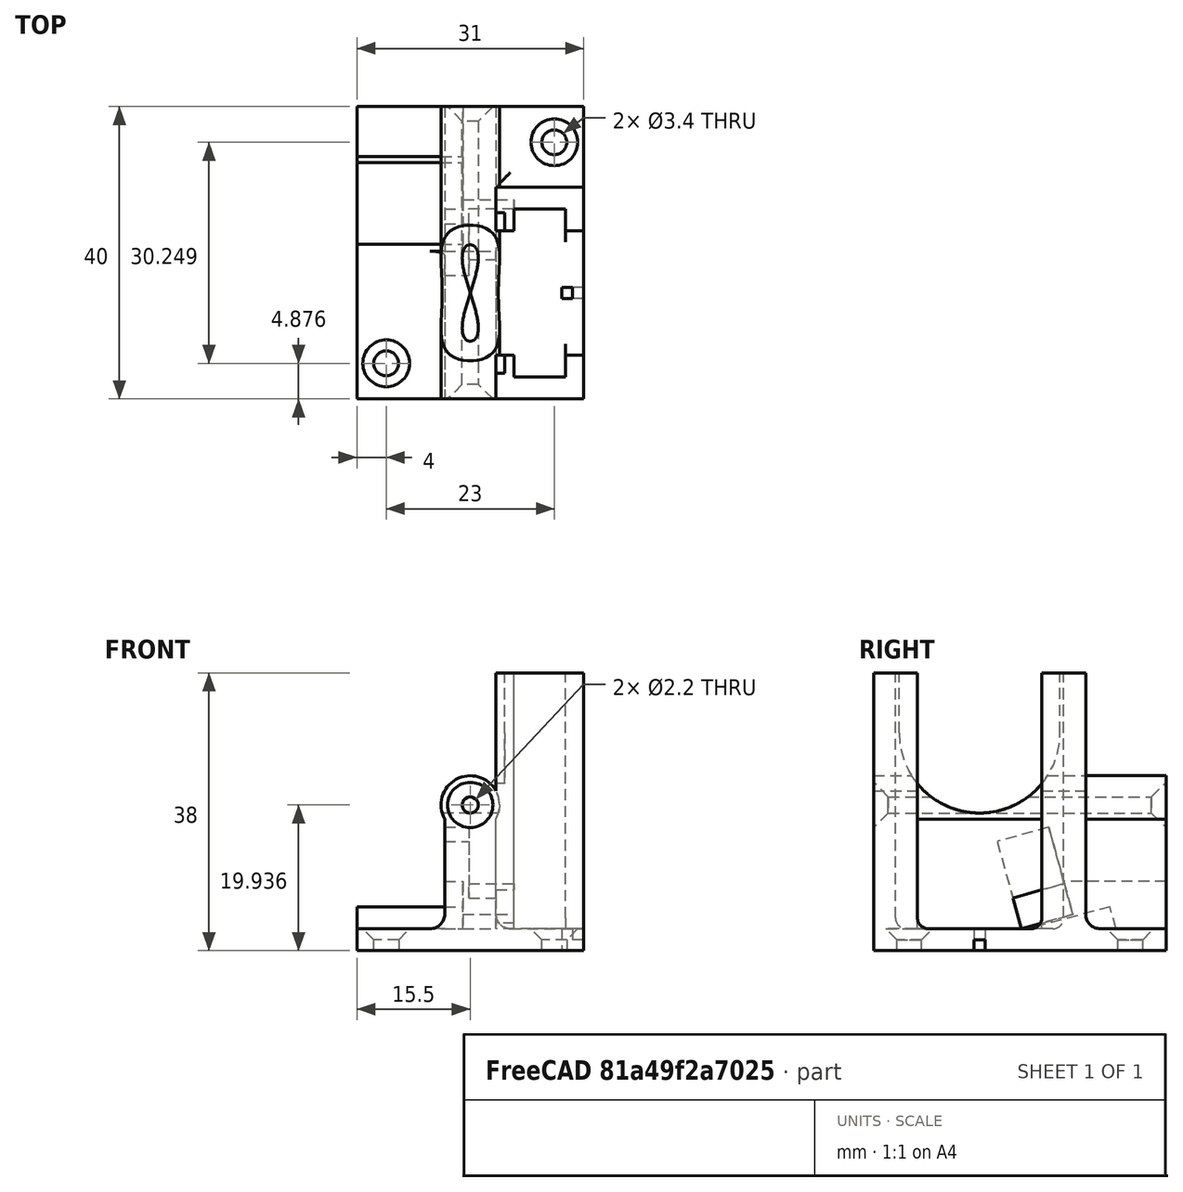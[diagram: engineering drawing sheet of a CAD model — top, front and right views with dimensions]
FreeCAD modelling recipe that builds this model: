
FCSTD DOCUMENT  (FreeCAD 0.20RUnknown)
Label: MainBody
License: All rights reserved
LicenseURL: http://en.wikipedia.org/wiki/All_rights_reserved
objects: Sketcher::SketchObject×10, PartDesign::Pocket×7, PartDesign::Pad×3, PartDesign::Fillet×2, PartDesign::Chamfer×2, Mesh::Feature×1, App::Part×1, PartDesign::Body×1
note: 39 computed .brp shape members not serialized (recipe doc carries the construction recipe); baked Part::Feature solids carry a one-line shape summary decoded from their .brp
EXTERNAL_REF file=SharedParameters.FCStd obj=Spreadsheet

FEATURE [Sketcher::SketchObject] Sketch  label="MainBodySketch"
  FullyConstrained = true
  MapMode = 5
  Placement = pos=(0,0,0) rot=(1,0,0;1.5708rad)
  Support = -> [XZ_Plane]
  expr: Constraints[19] = <<SharedParameters>>#<<Parameters>>.WallThinkness
  expr: Constraints[20] = <<SharedParameters>>#<<Parameters>>.FilamentWheel_BaseWidth
  sketch-geometry (9):
    g0: LineSegment StartX=-15.5 StartY=0 StartZ=0 EndX=-15.5 EndY=3 EndZ=0
    g1: LineSegment StartX=-15.5 StartY=3 StartZ=0 EndX=-3.5 EndY=3 EndZ=0
    g2: LineSegment StartX=-3.5 StartY=3 StartZ=0 EndX=-3.5 EndY=18 EndZ=0
    g3: LineSegment StartX=-15.5 StartY=0 StartZ=0 EndX=15.5 EndY=0 EndZ=0
    g4: LineSegment StartX=15.5 StartY=0 StartZ=0 EndX=15.5 EndY=3 EndZ=0
    g5: LineSegment StartX=15.5 StartY=3 StartZ=0 EndX=3.5 EndY=3 EndZ=0
    g6: LineSegment StartX=3.5 StartY=3 StartZ=0 EndX=3.5 EndY=18 EndZ=0
    g7: ArcOfCircle CenterX=-5e-16 CenterY=19.9365 CenterZ=0 NormalX=0 NormalY=0 NormalZ=1 AngleXU=0 Radius=4 StartAngle=5.77782 EndAngle=9.93014
    g8: Circle CenterX=-5e-16 CenterY=19.9365 CenterZ=0 NormalX=0 NormalY=0 NormalZ=1 AngleXU=0 Radius=1.1
  constraints (26):
    c: PointOnObject(g0,g-1)
    c: Vertical(g0)
    c: Coincident(g0,g1)
    c: Horizontal(g1)
    c: Coincident(g1,g2)
    c: Vertical(g2)
    c: Coincident(g0,g3)
    c: Coincident(g3,g4)
    c: Coincident(g4,g5)
    c: Horizontal(g5)
    c: Coincident(g5,g6)
    c: Vertical(g4)
    c: Symmetric(g0,g3,g-2)
    c: Vertical(g6)
    c: Horizontal(g6,g2)
    c: Symmetric(g5,g1,g-2)
    c: Coincident(g7,g2)
    c: Coincident(g7,g6)
    c: Coincident(g8,g7)
    c: DistanceY(g0,g0) = 3
    c: DistanceX(g3,g3) = 31
    c: DistanceX(g1,g5) = 7  'FilamentTubeTowerThinkness'
    c: DistanceY(g2,g2) = 15
    c: Diameter(g8) = 2.2  'FilamentHoleDiameter'
    c: Diameter(g7) = 8  'FilementHoleOuterDia'
    c: DistanceY(g7) = 19.9365  'FilementHoleCenterHeight'
FEATURE [PartDesign::Pad] Pad  label="MainBodyPad"
  Direction = (0,-1,-2e-16)
  Length = 40
  Length2 = 10
  Placement = pos=(0,0,0) rot=(1,0,0;1.5708rad)
  Profile = -> Sketch
  ReferenceAxis = -> Sketch [N_Axis]
  Refine = true
  Type = 0
  expr: Length = <<SharedParameters>>#<<Parameters>>.FilamentWheel_BaseLength
FEATURE [Sketcher::SketchObject] Sketch001  label="SupportGuidesSketch"
  AttachmentOffset = pos=(0,0,3) rot=(0,0,1;0rad)
  FullyConstrained = true
  MapMode = 5
  Placement = pos=(0,0,3) rot=(0,0,1;0rad)
  Support = -> [XY_Plane]
  expr: .AttachmentOffset.Base.z = <<SharedParameters>>#<<Parameters>>.WallThinkness
  expr: .Constraints.SupportGuidesLength = <<SharedParameters>>#<<Parameters>>.FilamentWheel_SupportWidth
  expr: .Constraints.WallThinkness = <<SharedParameters>>#<<Parameters>>.FilamentWheel_SupportWallThinkness
  expr: Constraints[41] = -<<SharedParameters>>#<<Parameters>>.FilamentWheel_BaseLength
  expr: Constraints[42] = <<SharedParameters>>#<<Parameters>>.FilamentWheel_BaseWidth / 2
  expr: Constraints[43] = <<SharedParameters>>#<<Parameters>>.FilamentWheel_SupportTeethWidth
  expr: Constraints[45] = <<SharedParameters>>#<<Parameters>>.WallThinkness
  expr: Constraints[46] = <<SharedParameters>>#<<Parameters>>.WallThinkness
  sketch-geometry (16):
    g0: LineSegment StartX=3.5 StartY=-40 StartZ=0 EndX=15.5 EndY=-40 EndZ=0
    g1: LineSegment StartX=15.5 StartY=-40 StartZ=0 EndX=15.5 EndY=-34 EndZ=0
    g2: LineSegment StartX=15.5 StartY=-34 StartZ=0 EndX=13 EndY=-34 EndZ=0
    g3: LineSegment StartX=13 StartY=-34 StartZ=0 EndX=13 EndY=-37 EndZ=0
    g4: LineSegment StartX=13 StartY=-37 StartZ=0 EndX=6 EndY=-37 EndZ=0
    g5: LineSegment StartX=6 StartY=-37 StartZ=0 EndX=6 EndY=-34 EndZ=0
    g6: LineSegment StartX=6 StartY=-34 StartZ=0 EndX=3.5 EndY=-34 EndZ=0
    g7: LineSegment StartX=3.5 StartY=-34 StartZ=0 EndX=3.5 EndY=-40 EndZ=0
    g8: LineSegment StartX=3.5 StartY=-17 StartZ=0 EndX=3.5 EndY=-11 EndZ=0
    g9: LineSegment StartX=3.5 StartY=-11 StartZ=0 EndX=15.5 EndY=-11 EndZ=0
    g10: LineSegment StartX=15.5 StartY=-11 StartZ=0 EndX=15.5 EndY=-17 EndZ=0
    g11: LineSegment StartX=15.5 StartY=-17 StartZ=0 EndX=13 EndY=-17 EndZ=0
    g12: LineSegment StartX=13 StartY=-17 StartZ=0 EndX=13 EndY=-14 EndZ=0
    g13: LineSegment StartX=13 StartY=-14 StartZ=0 EndX=6 EndY=-14 EndZ=0
    g14: LineSegment StartX=6 StartY=-14 StartZ=0 EndX=6 EndY=-17 EndZ=0
    g15: LineSegment StartX=6 StartY=-17 StartZ=0 EndX=3.5 EndY=-17 EndZ=0
  constraints (49):
    c: Horizontal(g0)
    c: Coincident(g0,g1)
    c: Vertical(g1)
    c: Coincident(g1,g2)
    c: Coincident(g2,g3)
    c: Coincident(g3,g4)
    c: Coincident(g4,g5)
    c: Coincident(g5,g6)
    c: Horizontal(g6)
    c: Coincident(g6,g7)
    c: Coincident(g7,g0)
    c: Vertical(g8)
    c: Coincident(g8,g9)
    c: Horizontal(g9)
    c: Coincident(g9,g10)
    c: Vertical(g10)
    c: Coincident(g10,g11)
    c: Coincident(g11,g12)
    c: Coincident(g12,g13)
    c: Horizontal(g13)
    c: Coincident(g13,g14)
    c: Coincident(g14,g15)
    c: Coincident(g15,g8)
    c: Horizontal(g15)
    c: Horizontal(g2)
    c: Horizontal(g4)
    c: Vertical(g5)
    c: Vertical(g3)
    c: Vertical(g12)
    c: Vertical(g14)
    c: Vertical(g7)
    c: Vertical(g6,g8)
    c: Horizontal(g11)
    c: Horizontal(g2,g5)
    c: Horizontal(g14,g11)
    c: Vertical(g1,g10)
    c: Vertical(g14,g5)
    c: Vertical(g2,g11)
    c: Equal(g5,g14)
    c: Equal(g6,g2)
    c: Equal(g8,g7)
    c: DistanceY(g0) = -40
    c: DistanceX(g0) = 15.5
    c: DistanceX(g4,g4) = 7
    c: DistanceX(g6,g6) = 2.5  'WallThinkness'
    c: DistanceY(g3,g3) = 3
    c: DistanceY(g0,g3) = 3
    c: DistanceY(g3,g12) = 23  'SupportGuidesLength'
    c: DistanceX(g9,g9) = 12  'SupportGuidesWidth'
FEATURE [PartDesign::Pad] Pad001  label="SupportGuidesPad"
  BaseFeature = -> Pad
  Direction = (0,0,1)
  Length = 35
  Length2 = 10
  Placement = pos=(0,0,0) rot=(1,0,0;1.5708rad)
  Profile = -> Sketch001
  ReferenceAxis = -> Sketch001 [N_Axis]
  Refine = true
  Type = 0
FEATURE [Sketcher::SketchObject] Sketch002  label="RibberRingWheelSpacerSketch"
  AttachmentOffset = pos=(0,0,-3.5) rot=(0,0,1;0rad)
  FullyConstrained = true
  MapMode = 5
  Placement = pos=(3.5,-8e-16,8e-16) rot=(-0.57735,0.57735,0.57735;4.18879rad)
  Support = -> [YZ_Plane]
  expr: .AttachmentOffset.Base.z = -<<SharedParameters>>#<<Parameters>>.FilamentWheel_BaseWidth / 2 + <<SupportGuidesSketch>>.Constraints.SupportGuidesWidth
  expr: Constraints[11] = <<MainBodySketch>>.Constraints.FilementHoleCenterHeight - <<MainBodySketch>>.Constraints.FilamentHoleDiameter / 2
  expr: Constraints[12] = <<MainBodyPad>>.Length
  expr: Constraints[7] = <<SharedParameters>>#<<Parameters>>.FilementWheel_RibberWheelContactRadius + 1mm
  expr: Constraints[8] = <<SharedParameters>>#<<Parameters>>.FilamentWheel_BaseLength - <<SharedParameters>>#<<Parameters>>.WallThinkness - <<SharedParameters>>#<<Parameters>>.FilamentWheel_SupportWidth / 2
  sketch-geometry (5):
    g0: LineSegment StartX=14.5 StartY=29.8365 StartZ=0 EndX=14.5 EndY=40 EndZ=0
    g1: LineSegment StartX=14.5 StartY=40 StartZ=0 EndX=36.5 EndY=40 EndZ=0
    g2: LineSegment StartX=36.5 StartY=40 StartZ=0 EndX=36.5 EndY=29.8365 EndZ=0
    g3: ArcOfCircle CenterX=25.5 CenterY=29.8365 CenterZ=0 NormalX=0 NormalY=0 NormalZ=1 AngleXU=0 Radius=11 StartAngle=3.14159 EndAngle=6.28319
    g4: GeomPoint X=25.5 Y=18.8365 Z=0
  constraints (13):
    c: Vertical(g0)
    c: Coincident(g0,g1)
    c: Horizontal(g1)
    c: Coincident(g1,g2)
    c: Vertical(g2)
    c: Tangent(g3,g2) = 1.5708
    c: Tangent(g3,g0) = 1.5708
    c: Radius(g3) = 11
    c: DistanceX(g-1,g3) = 25.5
    c: PointOnObject(g4,g3)
    c: Vertical(g4,g3)
    c: DistanceY(g-1,g4) = 18.8365
    c: DistanceY(g0) = 40
FEATURE [PartDesign::Pocket] Pocket  label="RibberRingWheelSpacerPocket"
  BaseFeature = -> Pad001
  Direction = (1,-2e-16,3e-16)
  Length = 1.2
  Length2 = 8
  Placement = pos=(0,0,0) rot=(1,0,0;1.5708rad)
  Profile = -> Sketch002
  ReferenceAxis = -> Sketch002 [N_Axis]
  Refine = true
  Type = 4
  expr: Length2 = <<MainBodySketch>>.Constraints.FilementHoleOuterDia
FEATURE [Sketcher::SketchObject] Sketch003  label="SensorSpacerSketch"
  AttachmentOffset = pos=(0,0,3.5) rot=(0,0,1;0rad)
  FullyConstrained = true
  MapMode = 5
  Placement = pos=(-3.5,8e-16,-8e-16) rot=(-0.57735,0.57735,0.57735;4.18879rad)
  Support = -> [YZ_Plane]
  expr: .AttachmentOffset.Base.z = <<MainBodySketch>>.Constraints.FilamentTubeTowerThinkness / 2
  expr: Constraints[10] = <<SharedParameters>>#<<Parameters>>.WallThinkness
  sketch-geometry (6):
    g0: LineSegment StartX=0 StartY=9.5 StartZ=0 EndX=14 EndY=9.5 EndZ=0
    g1: LineSegment StartX=14 StartY=9.5 StartZ=0 EndX=16.0522 EndY=16.8999 EndZ=0
    g2: LineSegment StartX=16.0522 StartY=16.8999 StartZ=0 EndX=23.0867 EndY=14.949 EndZ=0
    g3: LineSegment StartX=23.0867 StartY=14.949 StartZ=0 EndX=19.7729 EndY=3 EndZ=0
    g4: LineSegment StartX=19.7729 StartY=3 StartZ=0 EndX=0 EndY=3 EndZ=0
    g5: LineSegment StartX=0 StartY=3 StartZ=0 EndX=0 EndY=9.5 EndZ=0
  constraints (18):
    c: Horizontal(g0)
    c: Coincident(g0,g1)
    c: Coincident(g1,g2)
    c: Coincident(g2,g3)
    c: Coincident(g3,g4)
    c: PointOnObject(g4,g-2)
    c: Horizontal(g4)
    c: Coincident(g4,g5)
    c: Coincident(g5,g0)
    c: Vertical(g5)
    c: DistanceY(g4) = 3
    c: Parallel(g1,g3)
    c: Perpendicular(g2,g1)
    c: Distance(g2) = 7.3
    c: Angle(g1,g0) = 1.84132
    c: DistanceX(g0,g0) = 14
    c: DistanceY(g5,g5) = 6.5
    c: Distance(g3) = 12.4
FEATURE [Mesh::Feature] Mesh002  label="MovementSensor (Meshed)"
  Placement = pos=(7,-24.4225,4.56263) rot=(0,0.139173,0.990268;3.14159rad)
FEATURE [App::Part] Part
  Group = -> [Mesh002]
  Origin = -> Origin001
  Placement = pos=(-0.4,-40.7,0) rot=(0,0,-1;3.14159rad)
FEATURE [PartDesign::Pocket] Pocket001  label="SensorSpacerPocket"
  BaseFeature = -> Pocket
  Direction = (1,-2e-16,3e-16)
  Length = 2.5
  Length2 = 5
  Placement = pos=(0,0,0) rot=(1,0,0;1.5708rad)
  Profile = -> Sketch003
  ReferenceAxis = -> Sketch003 [N_Axis]
  Refine = true
  Type = 0
FEATURE [Sketcher::SketchObject] Sketch004  label="SensorSpacerSketch002"
  AttachmentOffset = pos=(0,0,3.5) rot=(0,0,1;0rad)
  ExternalGeometry = -> [Sketch003]
  FullyConstrained = true
  MapMode = 5
  Placement = pos=(-3.5,8e-16,-8e-16) rot=(-0.57735,0.57735,0.57735;4.18879rad)
  Support = -> [YZ_Plane]
  expr: .AttachmentOffset.Base.z = <<MainBodySketch>>.Constraints.FilamentTubeTowerThinkness / 2
  sketch-geometry (4):
    g0: LineSegment StartX=16.0522 StartY=16.8999 StartZ=0 EndX=13.7005 EndY=8.41991 EndZ=0
    g1: LineSegment StartX=16.0522 StartY=16.8999 StartZ=0 EndX=23.0867 EndY=14.949 EndZ=0
    g2: LineSegment StartX=23.0867 StartY=14.949 StartZ=0 EndX=20.735 EndY=6.46907 EndZ=0
    g3: LineSegment StartX=20.735 StartY=6.46907 StartZ=0 EndX=13.7005 EndY=8.41991 EndZ=0
  constraints (10):
    c: Coincident(g0,g-4)
    c: Coincident(g1,g0)
    c: Coincident(g1,g-5)
    c: Coincident(g2,g1)
    c: PointOnObject(g2,g-5)
    c: Coincident(g3,g2)
    c: Coincident(g3,g0)
    c: Perpendicular(g2,g3)
    c: Parallel(g-4,g0)
    c: Distance(g0) = 8.8
FEATURE [PartDesign::Pocket] Pocket002  label="SensorSpacerPocket002"
  BaseFeature = -> Pocket001
  Direction = (1,-2e-16,3e-16)
  Length = 3.3
  Length2 = 5
  Placement = pos=(0,0,0) rot=(1,0,0;1.5708rad)
  Profile = -> Sketch004
  ReferenceAxis = -> Sketch004 [N_Axis]
  Refine = true
  Type = 0
FEATURE [Sketcher::SketchObject] Sketch005  label="SensorSpacerSketch003"
  AttachmentOffset = pos=(0,0,3.5) rot=(0,0,1;0rad)
  ExternalGeometry = -> [Sketch003]
  FullyConstrained = false
  MapMode = 5
  Placement = pos=(-3.5,8e-16,-8e-16) rot=(-0.57735,0.57735,0.57735;4.18879rad)
  Support = -> [YZ_Plane]
  expr: .AttachmentOffset.Base.z = <<MainBodySketch>>.Constraints.FilamentTubeTowerThinkness / 2
  sketch-geometry (4):
    g0: LineSegment StartX=13.9088 StartY=9.17116 StartZ=0 EndX=20.9433 EndY=7.22032 EndZ=0
    g1: LineSegment StartX=20.9433 StartY=7.22032 StartZ=0 EndX=19.7729 EndY=3 EndZ=0
    g2: LineSegment StartX=19.7729 StartY=3 StartZ=0 EndX=12.7384 EndY=4.95084 EndZ=0
    g3: LineSegment StartX=12.7384 StartY=4.95084 StartZ=0 EndX=13.9088 EndY=9.17116 EndZ=0
  constraints (10):
    c: Coincident(g0,g1)
    c: Coincident(g1,g2)
    c: Coincident(g2,g3)
    c: Coincident(g3,g0)
    c: Parallel(g0,g-3)
    c: Parallel(g1,g3)
    c: Perpendicular(g0,g3)
    c: Coincident(g-4,g1)
    c: Parallel(g2,g0)
    c: PointOnObject(g0,g-5)
FEATURE [PartDesign::Pocket] Pocket003
  BaseFeature = -> Pocket002
  Direction = (1,-2e-16,3e-16)
  Length = 9.5
  Length2 = 5
  Placement = pos=(0,0,0) rot=(1,0,0;1.5708rad)
  Profile = -> Sketch005
  ReferenceAxis = -> Sketch005 [N_Axis]
  Refine = true
  Type = 0
  expr: Length = <<MainBodySketch>>.Constraints.FilamentTubeTowerThinkness + <<SupportGuidesSketch>>.Constraints.WallThinkness
FEATURE [Sketcher::SketchObject] Sketch006  label="SensorSupportSketch"
  AttachmentOffset = pos=(0,0,15.5) rot=(0,0,1;0rad)
  FullyConstrained = true
  MapMode = 5
  Placement = pos=(-15.5,3.4e-15,-3.4e-15) rot=(-0.57735,0.57735,0.57735;4.18879rad)
  Support = -> [YZ_Plane]
  expr: .AttachmentOffset.Base.z = <<SharedParameters>>#<<Parameters>>.FilamentWheel_BaseWidth / 2
  expr: Constraints[5] = <<SharedParameters>>#<<Parameters>>.WallThinkness
  sketch-geometry (3):
    g0: LineSegment StartX=6.85 StartY=3 StartZ=0 EndX=7.65385 EndY=6 EndZ=0
    g1: LineSegment StartX=18.85 StartY=3 StartZ=0 EndX=6.85 EndY=3 EndZ=0
    g2: LineSegment StartX=7.65385 StartY=6 StartZ=0 EndX=18.85 EndY=3 EndZ=0
  constraints (9):
    c: Coincident(g2,g0)
    c: Coincident(g2,g1)
    c: Coincident(g1,g0)
    c: Perpendicular(g2,g0)
    c: Horizontal(g1)
    c: DistanceY(g0) = 3
    c: Angle(g2,g1) = 0.261799
    c: DistanceX(g1,g1) = 12
    c: DistanceX(g0) = 6.85
FEATURE [PartDesign::Pad] Pad002  label="SensorSupportSketchPad"
  BaseFeature = -> Pocket003
  Direction = (-1,2e-16,-3e-16)
  Length = 19
  Length2 = 10
  Placement = pos=(0,0,0) rot=(1,0,0;1.5708rad)
  Profile = -> Sketch006
  ReferenceAxis = -> Sketch006 [N_Axis]
  Refine = true
  Reversed = true
  Type = 0
  expr: Length = <<SharedParameters>>#<<Parameters>>.FilamentWheel_BaseWidth / 2 + <<MainBodySketch>>.Constraints.FilamentTubeTowerThinkness / 2
FEATURE [Sketcher::SketchObject] Sketch007  label="RubberHoleSketch001"
  AttachmentOffset = pos=(0,0,3) rot=(0,0,1;0rad)
  FullyConstrained = true
  MapMode = 5
  Placement = pos=(0,0,3) rot=(0,0,1;0rad)
  Support = -> [XY_Plane]
  expr: .AttachmentOffset.Base.z = SharedParameters#<<Parameters>>.WallThinkness
  expr: .Constraints.DistanceY = -(SharedParameters#<<Parameters>>.FilamentWheel_BaseLength - <<SupportGuidesSketch>>.Constraints.SupportGuidesLength / 2 - <<SharedParameters>>#<<Parameters>>.WallThinkness + .Constraints.HoleSize / 2)
  expr: .Constraints.HoleSize = SharedParameters#<<Parameters>>.WallThinkness / 2
  expr: Constraints[10] = SharedParameters#<<Parameters>>.FilamentWheel_BaseWidth / 2 - .Constraints.HoleSize
  sketch-geometry (4):
    g0: LineSegment StartX=12.5 StartY=-24.75 StartZ=0 EndX=14 EndY=-24.75 EndZ=0
    g1: LineSegment StartX=14 StartY=-24.75 StartZ=0 EndX=14 EndY=-26.25 EndZ=0
    g2: LineSegment StartX=14 StartY=-26.25 StartZ=0 EndX=12.5 EndY=-26.25 EndZ=0
    g3: LineSegment StartX=12.5 StartY=-26.25 StartZ=0 EndX=12.5 EndY=-24.75 EndZ=0
  constraints (12):
    c: Coincident(g0,g1)
    c: Coincident(g1,g2)
    c: Coincident(g2,g3)
    c: Coincident(g3,g0)
    c: Horizontal(g0)
    c: Horizontal(g2)
    c: Vertical(g1)
    c: Vertical(g3)
    c: Equal(g3,g0)
    c: DistanceX(g0,g0) = 1.5  'HoleSize'
    c: DistanceX(g0) = 14
    c: DistanceY(g2) = -26.25  'DistanceY'
FEATURE [PartDesign::Pocket] Pocket004
  BaseFeature = -> Pad002
  Direction = (0,0,-1)
  Length = 5
  Length2 = 5
  Placement = pos=(0,0,0) rot=(1,0,0;1.5708rad)
  Profile = -> Sketch007
  ReferenceAxis = -> Sketch007 [N_Axis]
  Refine = true
  Type = 1
FEATURE [Sketcher::SketchObject] Sketch008  label="RubberHoleSketch002"
  AttachmentOffset = pos=(0,0,15.5) rot=(0,0,1;0rad)
  FullyConstrained = true
  MapMode = 5
  Placement = pos=(15.5,-3.4e-15,3.4e-15) rot=(0.57735,0.57735,0.57735;2.0944rad)
  Support = -> [YZ_Plane]
  expr: .AttachmentOffset.Base.z = <<SharedParameters>>#<<Parameters>>.FilamentWheel_BaseWidth / 2
  expr: Constraints[10] = <<RubberHoleSketch001>>.Constraints.HoleSize
  expr: Constraints[11] = <<RubberHoleSketch001>>.Constraints.DistanceY
  sketch-geometry (4):
    g0: LineSegment StartX=-26.25 StartY=1.5 StartZ=0 EndX=-24.75 EndY=1.5 EndZ=0
    g1: LineSegment StartX=-24.75 StartY=1.5 StartZ=0 EndX=-24.75 EndY=0 EndZ=0
    g2: LineSegment StartX=-24.75 StartY=0 StartZ=0 EndX=-26.25 EndY=0 EndZ=0
    g3: LineSegment StartX=-26.25 StartY=0 StartZ=0 EndX=-26.25 EndY=1.5 EndZ=0
  constraints (12):
    c: Coincident(g0,g1)
    c: Coincident(g1,g2)
    c: Coincident(g2,g3)
    c: Coincident(g3,g0)
    c: Horizontal(g0)
    c: Horizontal(g2)
    c: Vertical(g1)
    c: Vertical(g3)
    c: PointOnObject(g2,g-1)
    c: Equal(g3,g0)
    c: DistanceX(g0,g0) = 1.5
    c: DistanceX(g2) = -26.25
FEATURE [PartDesign::Pocket] Pocket005
  BaseFeature = -> Pocket004
  Direction = (-1,2e-16,-3e-16)
  Length = 3
  Length2 = 5
  Placement = pos=(0,0,0) rot=(1,0,0;1.5708rad)
  Profile = -> Sketch008
  ReferenceAxis = -> Sketch008 [N_Axis]
  Refine = true
  Type = 0
  expr: Length = <<SharedParameters>>#<<Parameters>>.WallThinkness
FEATURE [Sketcher::SketchObject] Sketch009  label="ScrewHolesSketch"
  AttachmentOffset = pos=(0,0,3) rot=(0,0,1;0rad)
  FullyConstrained = true
  MapMode = 5
  Placement = pos=(0,0,3) rot=(0,0,1;0rad)
  Support = -> [XY_Plane]
  expr: .AttachmentOffset.Base.z = <<SharedParameters>>#<<Parameters>>.WallThinkness
  expr: Constraints[4] = -<<SharedParameters>>#<<Parameters>>.FilamentWheel_BaseLength / 2
  expr: Constraints[6] = <<SharedParameters>>#<<Parameters>>.FilamentWheel_BaseWidth / 2 - 4mm
  sketch-geometry (3):
    g0: Circle CenterX=-11.5 CenterY=-35.1245 CenterZ=0 NormalX=0 NormalY=0 NormalZ=1 AngleXU=0 Radius=1.7
    g1: Circle CenterX=11.5 CenterY=-4.87552 CenterZ=0 NormalX=0 NormalY=0 NormalZ=1 AngleXU=0 Radius=1.7
    g2: GeomPoint X=0 Y=-20 Z=0
  constraints (7):
    c: Equal(g1,g0)
    c: Diameter(g1) = 3.4
    c: Distance(g0,g1) = 38
    c: PointOnObject(g2,g-2)
    c: DistanceY(g2) = -20
    c: Symmetric(g0,g1,g2)
    c: DistanceX(g1) = 11.5
FEATURE [PartDesign::Pocket] Pocket006
  BaseFeature = -> Pocket005
  Direction = (0,0,-1)
  Length = 5
  Length2 = 5
  Placement = pos=(0,0,0) rot=(1,0,0;1.5708rad)
  Profile = -> Sketch009
  ReferenceAxis = -> Sketch009 [N_Axis]
  Refine = true
  Type = 1
FEATURE [PartDesign::Fillet] Fillet
  Base = -> Pocket006 [Edge155,Edge99,Edge94]
  BaseFeature = -> Pocket006
  Placement = pos=(0,0,0) rot=(1,0,0;1.5708rad)
  Radius = 2
  Refine = true
  SupportTransform = false
  UseAllEdges = false
FEATURE [PartDesign::Chamfer] Chamfer
  Angle = 45
  Base = -> Fillet [Edge33,Edge155]
  BaseFeature = -> Fillet
  ChamferType = 0
  FlipDirection = false
  Placement = pos=(0,0,0) rot=(1,0,0;1.5708rad)
  Refine = true
  Size = 1.5
  Size2 = 1
  SupportTransform = false
  UseAllEdges = false
FEATURE [PartDesign::Chamfer] Chamfer001
  Angle = 45
  Base = -> Chamfer [Edge124,Edge18]
  BaseFeature = -> Chamfer
  ChamferType = 0
  FlipDirection = false
  Placement = pos=(0,0,0) rot=(1,0,0;1.5708rad)
  Refine = true
  Size = 2
  Size2 = 1
  SupportTransform = false
  UseAllEdges = false
FEATURE [PartDesign::Fillet] Fillet001
  Base = -> Chamfer001 [Edge96,Edge93,Edge90,Edge92]
  BaseFeature = -> Chamfer001
  Placement = pos=(0,0,0) rot=(1,0,0;1.5708rad)
  Radius = 1.5
  Refine = true
  SupportTransform = false
  UseAllEdges = false
FEATURE [PartDesign::Body] Body  label="MainBody"
  Group = -> [Sketch,Pad,Sketch001,Pad001,Sketch002,Pocket,Sketch003,Pocket001,Sketch004,Pocket002,Sketch005,Pocket003,Sketch006,Pad002,Sketch007,Pocket004,Sketch008,Pocket005,Sketch009,Pocket006,Fillet,Chamfer,Chamfer001,Fillet001]
  Origin = -> Origin
  Tip = -> Fillet001
